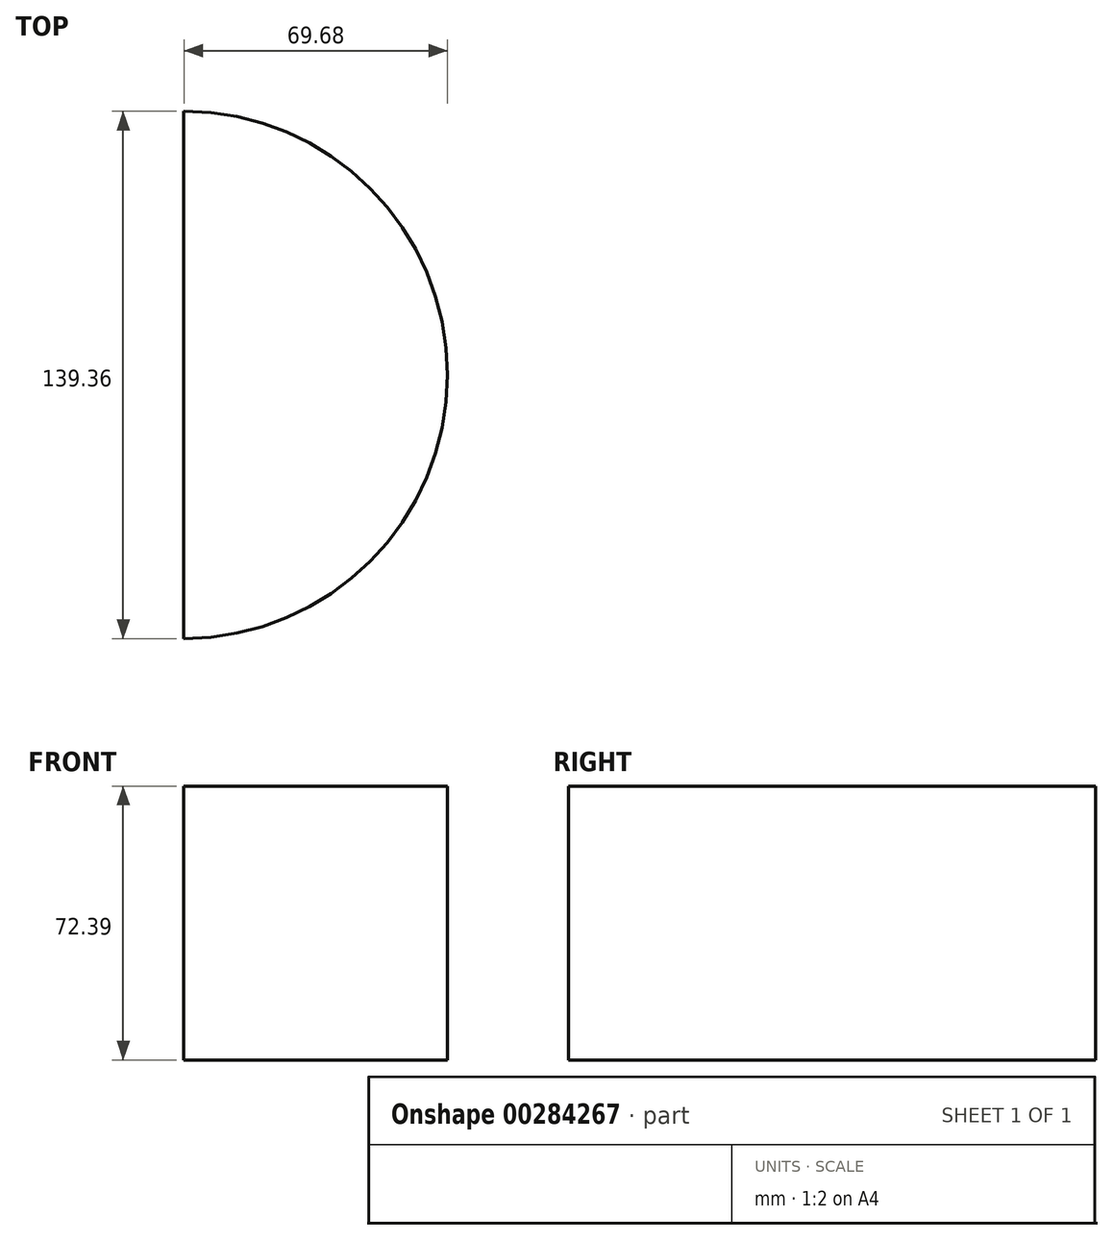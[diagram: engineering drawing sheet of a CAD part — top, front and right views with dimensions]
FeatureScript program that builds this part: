
annotation { "Feature Type Name" : "Feature", "Feature Type Description" : "" }
export const myFeature = defineFeature(function(context is Context, id is Id, definition is map)
    precondition{}
    {
        {
            var Q0;
            Q0=qCreatedBy(makeId("Top.planeOp"),FACE);
            var sketch = newSketch(context, id + "F0", { "sketchPlane" : qUnion([Q0])});
            skLineSegment(sketch, "E0.bottom", {"start": v(-73.97, 69.68) * mm, "end": v(72.57, 69.68) * mm});
            skLineSegment(sketch, "E0.top", {"start": v(-73.97, -69.68) * mm, "end": v(72.57, -69.68) * mm});
            skLineSegment(sketch, "E0.left", {"start": v(-73.97, 69.68) * mm, "end": v(-73.97, -69.68) * mm});
            skLineSegment(sketch, "E0.right", {"start": v(72.57, 69.68) * mm, "end": v(72.57, -69.68) * mm});
            skPoint(sketch, "E0.middle", {"position": v(-0.7, 0) * mm});
            skCircle(sketch, "E1", {"center": v(-73.97, 0) * mm, "radius": 69.68 * mm});
            skSolve(sketch);
        }
        {
            var Q0;
            {var subQ0=sQuery(id+"F0.wireOp",EDGE,"E0.left");Q0=makeQuery(id+"F0.imprint","IMPRINT",FACE,{"disambiguationData":[TD([[makeQuery(id+"F0.imprint","IMPRINT",EDGE,{"derivedFrom":subQ0}),1.0]])]});}
            extrude(context, id + "F1", {"entities" : qUnion([Q0]), "depth" : 72.39 * mm});
        }
    });
